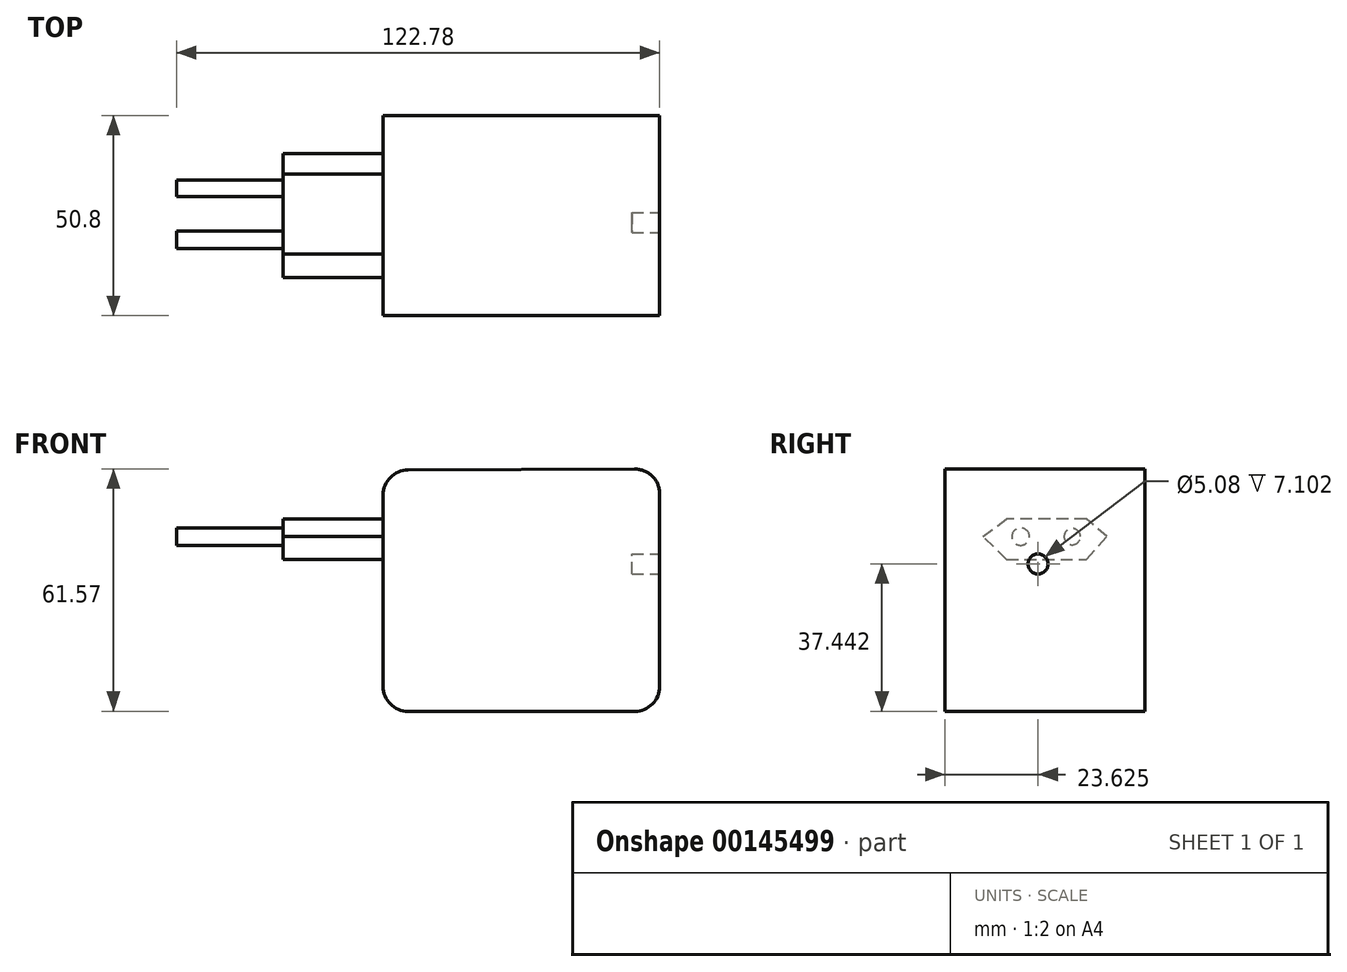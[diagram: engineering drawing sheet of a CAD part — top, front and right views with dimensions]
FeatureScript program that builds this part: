
annotation { "Feature Type Name" : "Feature", "Feature Type Description" : "" }
export const myFeature = defineFeature(function(context is Context, id is Id, definition is map)
    precondition{}
    {
        {
            var Q0;
            Q0=qCreatedBy(makeId("Front.planeOp"),FACE);
            var sketch = newSketch(context, id + "F0", { "sketchPlane" : qUnion([Q0])});
            skLineSegment(sketch, "E0", {"start": v(-40.08, 31.9) * mm, "end": v(-40.08, -16.7) * mm});
            skLineSegment(sketch, "E1", {"start": v(-33.73, -23.06) * mm, "end": v(23.83, -23.06) * mm});
            skLineSegment(sketch, "E2", {"start": v(30.18, -16.7) * mm, "end": v(30.18, 32.16) * mm});
            skLineSegment(sketch, "E3", {"start": v(23.8, 38.5) * mm, "end": v(-33.76, 38.25) * mm});
            skPoint(sketch, "E4.visualSharp", {"position": v(-40.08, -23.06) * mm});
            skArc(sketch, "E4.filletArc", {"start": v(-40.08, -16.7) * mm, "mid": v(-38.22, -21.2) * mm, "end": v(-33.73, -23.06) * mm});
            skPoint(sketch, "E5.visualSharp", {"position": v(-40.08, 38.23) * mm});
            skArc(sketch, "E5.filletArc", {"start": v(-33.76, 38.25) * mm, "mid": v(-38.23, 36.38) * mm, "end": v(-40.08, 31.9) * mm});
            skPoint(sketch, "E6.visualSharp", {"position": v(30.18, 38.53) * mm});
            skArc(sketch, "E6.filletArc", {"start": v(30.18, 32.16) * mm, "mid": v(28.3, 36.66) * mm, "end": v(23.8, 38.5) * mm});
            skPoint(sketch, "E7.visualSharp", {"position": v(30.18, -23.06) * mm});
            skArc(sketch, "E7.filletArc", {"start": v(23.83, -23.06) * mm, "mid": v(28.32, -21.2) * mm, "end": v(30.18, -16.7) * mm});
            skSolve(sketch);
        }
        {
            var Q0;
            Q0=makeQuery(id+"F0.imprint","IMPRINT",FACE,{"disambiguationData":[TD([[makeQuery(id+"F0.imprint","IMPRINT",EDGE,{"derivedFrom":sQuery(id+"F0.wireOp",EDGE,"E0")}),1.0]])]});
            extrude(context, id + "F1", {"entities" : qUnion([Q0]), "depth" : 50.8 * mm});
        }
        {
            var Q0;
            Q0=makeQuery(id+"F1.opExtrude","SWEPT_FACE",FACE,{"disambiguationData":[OSD([sQuery(id+"F0.wireOp",EDGE,"E0")])]});
            var sketch = newSketch(context, id + "F2", { "sketchPlane" : qUnion([Q0])});
            skLineSegment(sketch, "E8", {"start": v(9.63, 21.33) * mm, "end": v(14.88, 25.76) * mm});
            skLineSegment(sketch, "E9", {"start": v(14.88, 25.76) * mm, "end": v(35.2, 25.76) * mm});
            skLineSegment(sketch, "E10", {"start": v(41.1, 21.33) * mm, "end": v(35.2, 25.76) * mm});
            skLineSegment(sketch, "E11", {"start": v(14.88, 15.6) * mm, "end": v(9.63, 21.33) * mm});
            skLineSegment(sketch, "E12", {"start": v(35.2, 15.6) * mm, "end": v(14.88, 15.6) * mm});
            skLineSegment(sketch, "E13", {"start": v(35.2, 15.6) * mm, "end": v(41.1, 21.33) * mm});
            skCircle(sketch, "E14", {"center": v(18.48, 21.33) * mm, "radius": 2.07 * mm});
            skCircle(sketch, "E15", {"center": v(31.6, 21.33) * mm, "radius": 2.23 * mm});
            skSolve(sketch);
        }
        {
            var Q0;
            Q0 = qSketchRegion(id + "F2", true);
            extrude(context, id + "F3", {"entities" : qUnion([Q0]), "operationType" : NewBodyOperationType.ADD, "depth" : 25.4 * mm});
        }
        {
            var Q0;
            Q0=makeQuery(id+"F2.imprint","IMPRINT",FACE,{"disambiguationData":[TD([[makeQuery(id+"F2.imprint","IMPRINT",EDGE,{"derivedFrom":sQuery(id+"F2.wireOp",EDGE,"E14")}),1.0]])]});
            var Q1;
            Q1=makeQuery(id+"F2.imprint","IMPRINT",FACE,{"disambiguationData":[TD([[makeQuery(id+"F2.imprint","IMPRINT",EDGE,{"derivedFrom":sQuery(id+"F2.wireOp",EDGE,"E15")}),1.0]])]});
            extrude(context, id + "F4", {"entities" : qUnion([Q0, Q1]), "operationType" : NewBodyOperationType.ADD, "depth" : 52.5 * mm});
        }
        {
            var Q0;
            Q0=makeQuery(id+"F1.opExtrude","SWEPT_FACE",FACE,{"disambiguationData":[OSD([sQuery(id+"F0.wireOp",EDGE,"E2")])]});
            var sketch = newSketch(context, id + "F5", { "sketchPlane" : qUnion([Q0])});
            skCircle(sketch, "E16", {"center": v(-27.17, 14.38) * mm, "radius": 2.54 * mm});
            skSolve(sketch);
        }
        {
            var Q0;
            Q0=makeQuery(id+"F5.imprint","IMPRINT",FACE,{"disambiguationData":[TD([[makeQuery(id+"F5.imprint","IMPRINT",EDGE,{"derivedFrom":sQuery(id+"F5.wireOp",EDGE,"E16")}),1.0]])]});
            extrude(context, id + "F6", {"entities" : qUnion([Q0]), "operationType" : NewBodyOperationType.REMOVE, "oppositeDirection" : true, "depth" : 7.1 * mm});
        }
    });
